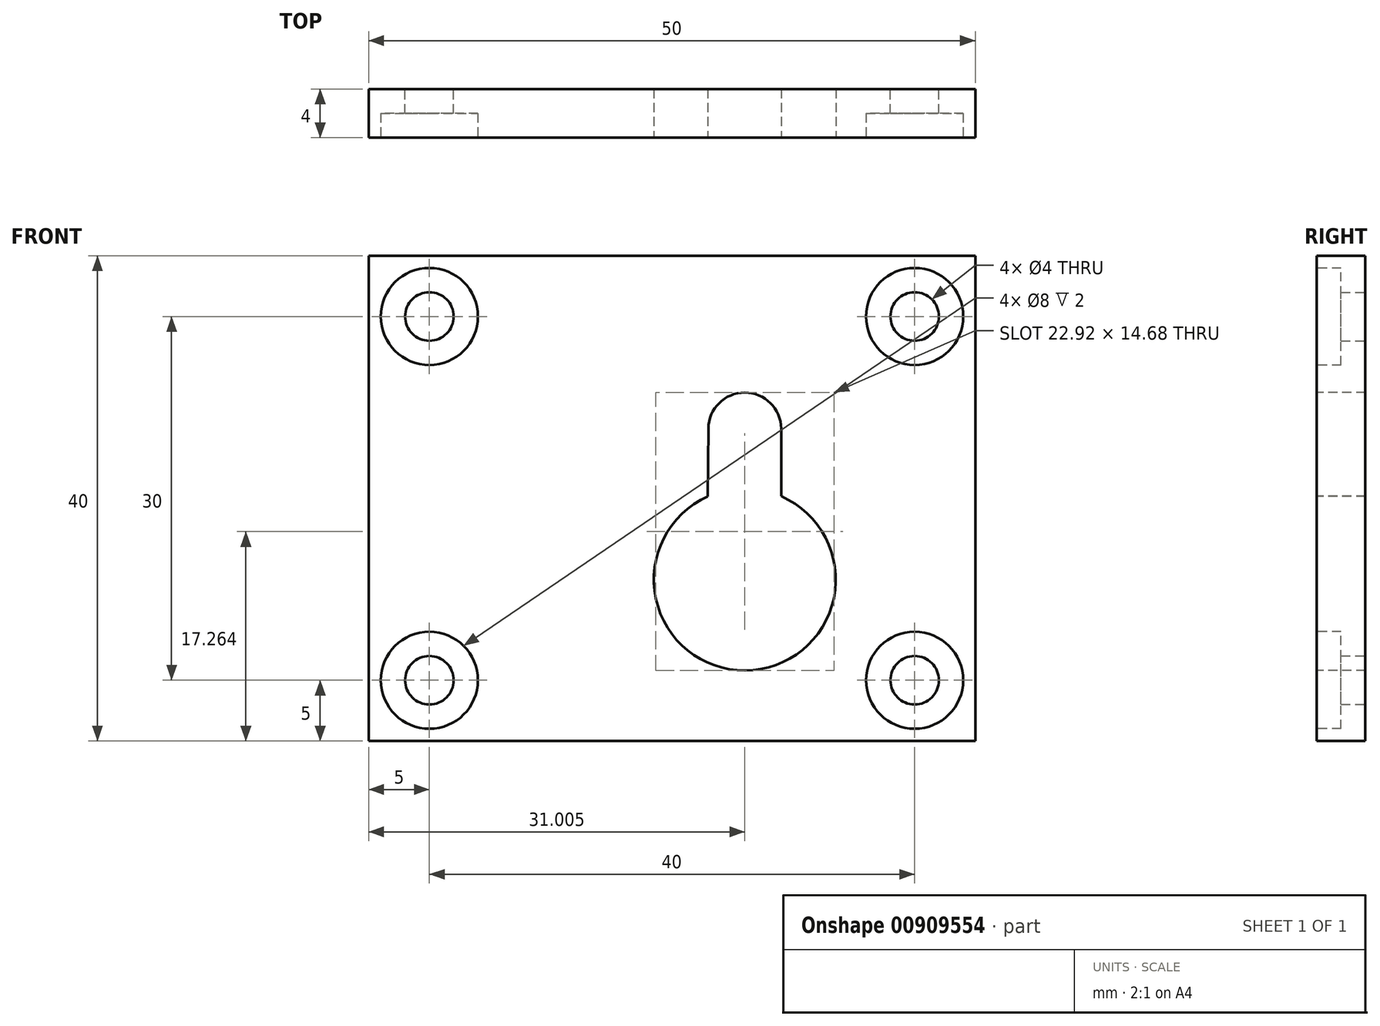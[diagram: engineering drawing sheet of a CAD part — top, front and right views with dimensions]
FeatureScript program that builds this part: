
annotation { "Feature Type Name" : "Feature", "Feature Type Description" : "" }
export const myFeature = defineFeature(function(context is Context, id is Id, definition is map)
    precondition{}
    {
        {
            var Q0;
            Q0=qCreatedBy(makeId("Front.planeOp"),FACE);
            var sketch = newSketch(context, id + "F0", { "sketchPlane" : qUnion([Q0])});
            skLineSegment(sketch, "E0.bottom", {"start": v(-25, 20) * mm, "end": v(25, 20) * mm});
            skLineSegment(sketch, "E0.top", {"start": v(-25, -20) * mm, "end": v(25, -20) * mm});
            skLineSegment(sketch, "E0.left", {"start": v(-25, 20) * mm, "end": v(-25, -20) * mm});
            skLineSegment(sketch, "E0.right", {"start": v(25, 20) * mm, "end": v(25, -20) * mm});
            skPoint(sketch, "E0.middle", {"position": v(0, 0) * mm});
            skCircle(sketch, "E1", {"center": v(-20, 15) * mm, "radius": 2 * mm});
            skCircle(sketch, "E2.0.1.0", {"center": v(-20, -15) * mm, "radius": 2 * mm});
            skCircle(sketch, "E2.1.0.0", {"center": v(20, 15) * mm, "radius": 2 * mm});
            skCircle(sketch, "E2.1.1.0", {"center": v(20, -15) * mm, "radius": 2 * mm});
            skLineSegment(sketch, "E2.direction1", {"start": v(-20, 15) * mm, "end": v(20, 15) * mm, "construction": true});
            skLineSegment(sketch, "E2.direction2", {"start": v(-20, 15) * mm, "end": v(-20, -15) * mm, "construction": true});
            skSolve(sketch);
        }
        {
            var Q0;
            Q0=makeQuery(id+"F0.imprint","IMPRINT",FACE,{"disambiguationData":[TD([[makeQuery(id+"F0.imprint","IMPRINT",EDGE,{"derivedFrom":sQuery(id+"F0.wireOp",EDGE,"E0.bottom")}),-1.0]])]});
            extrude(context, id + "F1", {"entities" : qUnion([Q0]), "depth" : 4 * mm, "offsetDistance" : 25 * mm});
        }
        {
            var Q0;
            Q0=makeQuery(id+"F1.opExtrude","CAP_FACE",FACE,{"disambiguationData":[OSD([sQuery(id+"F0.wireOp",EDGE,"E0.bottom"),sQuery(id+"F0.wireOp",EDGE,"E0.top"),sQuery(id+"F0.wireOp",EDGE,"E0.left"),sQuery(id+"F0.wireOp",EDGE,"E0.right"),sQuery(id+"F0.wireOp",EDGE,"E1"),sQuery(id+"F0.wireOp",EDGE,"E2.0.1.0"),sQuery(id+"F0.wireOp",EDGE,"E2.1.0.0"),sQuery(id+"F0.wireOp",EDGE,"E2.1.1.0")])],"isStart":false});
            var sketch = newSketch(context, id + "F2", { "sketchPlane" : qUnion([Q0])});
            skCircle(sketch, "E3", {"center": v(-20, 15) * mm, "radius": 4 * mm});
            skCircle(sketch, "E4.0.1.0", {"center": v(-20, -15) * mm, "radius": 4 * mm});
            skCircle(sketch, "E4.1.0.0", {"center": v(20, 15) * mm, "radius": 4 * mm});
            skCircle(sketch, "E4.1.1.0", {"center": v(20, -15) * mm, "radius": 4 * mm});
            skLineSegment(sketch, "E4.direction1", {"start": v(-20, 15) * mm, "end": v(20, 15) * mm, "construction": true});
            skLineSegment(sketch, "E4.direction2", {"start": v(-20, 15) * mm, "end": v(-20, -15) * mm, "construction": true});
            skSolve(sketch);
        }
        {
            var Q0;
            Q0=makeQuery(id+"F2.imprint","IMPRINT",FACE,{"disambiguationData":[TD([[makeQuery(id+"F2.imprint","IMPRINT",EDGE,{"derivedFrom":sQuery(id+"F2.wireOp",EDGE,"E3")}),1.0]])]});
            var Q1;
            Q1=makeQuery(id+"F2.imprint","IMPRINT",FACE,{"disambiguationData":[TD([[makeQuery(id+"F2.imprint","IMPRINT",EDGE,{"derivedFrom":sQuery(id+"F2.wireOp",EDGE,"E4.1.0.0")}),1.0]])]});
            var Q2;
            Q2=makeQuery(id+"F2.imprint","IMPRINT",FACE,{"disambiguationData":[TD([[makeQuery(id+"F2.imprint","IMPRINT",EDGE,{"derivedFrom":sQuery(id+"F2.wireOp",EDGE,"E4.1.1.0")}),1.0]])]});
            var Q3;
            Q3=makeQuery(id+"F2.imprint","IMPRINT",FACE,{"disambiguationData":[TD([[makeQuery(id+"F2.imprint","IMPRINT",EDGE,{"derivedFrom":sQuery(id+"F2.wireOp",EDGE,"E4.0.1.0")}),1.0]])]});
            extrude(context, id + "F3", {"entities" : qUnion([Q0, Q1, Q2, Q3]), "operationType" : NewBodyOperationType.REMOVE, "oppositeDirection" : true, "depth" : 2 * mm, "offsetDistance" : 25 * mm});
        }
        {
            var Q0;
            Q0=makeQuery(id+"F1.opExtrude","CAP_FACE",FACE,{"disambiguationData":[OSD([sQuery(id+"F0.wireOp",EDGE,"E0.bottom"),sQuery(id+"F0.wireOp",EDGE,"E0.top"),sQuery(id+"F0.wireOp",EDGE,"E0.left"),sQuery(id+"F0.wireOp",EDGE,"E0.right"),sQuery(id+"F0.wireOp",EDGE,"E1"),sQuery(id+"F0.wireOp",EDGE,"E2.0.1.0"),sQuery(id+"F0.wireOp",EDGE,"E2.1.0.0"),sQuery(id+"F0.wireOp",EDGE,"E2.1.1.0")])],"isStart":false});
            var sketch = newSketch(context, id + "F4", { "sketchPlane" : qUnion([Q0])});
            skLineSegment(sketch, "E5", {"start": v(-2.99, 5.98) * mm, "end": v(-3, 5.75) * mm});
            skLineSegment(sketch, "E6", {"start": v(3, 5.75) * mm, "end": v(3, 5.75) * mm});
            skArc(sketch, "E7", {"start": v(2.95, 0.16) * mm, "mid": v(6.03, -14.2) * mm, "end": v(9, 0.18) * mm});
            skArc(sketch, "E8", {"start": v(9, 5.7) * mm, "mid": v(6.02, 8.72) * mm, "end": v(3, 5.75) * mm});
            skArc(sketch, "E9.trimOffspring", {"start": v(-2.99, 5.98) * mm, "mid": v(-3, 5.87) * mm, "end": v(-3, 5.75) * mm});
            skPoint(sketch, "E10.end.orphan", {"position": v(2.99, 5.98) * mm});
            skPoint(sketch, "E11.orphan", {"position": v(-3.27, 0.05) * mm});
            skPoint(sketch, "E12.center.orphan", {"position": v(0, -6.7) * mm});
            skPoint(sketch, "E13.trimOffspring.end.orphan", {"position": v(3.27, 0.05) * mm});
            skLineSegment(sketch, "E14", {"start": v(9, 5.75) * mm, "end": v(9, 0.18) * mm});
            skLineSegment(sketch, "E15", {"start": v(3, 5.75) * mm, "end": v(2.95, 0.16) * mm});
            skSolve(sketch);
        }
        {
            var Q0;
            {var subQ1=sQuery(id+"F4.wireOp",EDGE,"E7");Q0=makeQuery(id+"F4.imprint","IMPRINT",FACE,{"disambiguationData":[TD([[makeQuery(id+"F4.imprint","IMPRINT",EDGE,{"derivedFrom":subQ1}),1.0]])]});}
            extrude(context, id + "F5", {"entities" : qUnion([Q0]), "operationType" : NewBodyOperationType.REMOVE, "oppositeDirection" : true, "depth" : 25 * mm, "offsetDistance" : 25 * mm});
        }
    });
